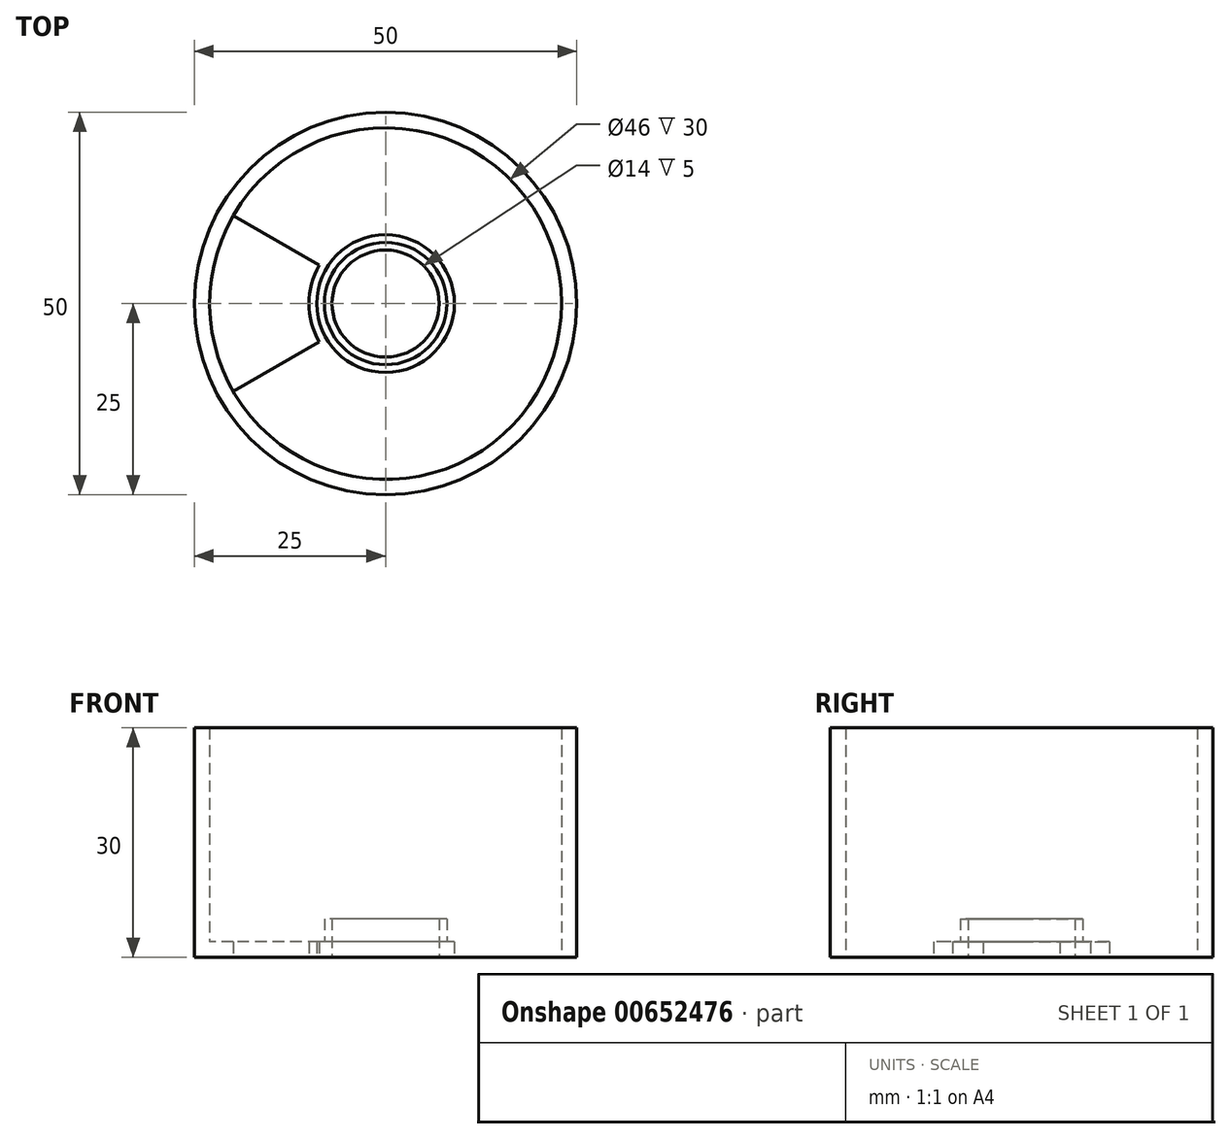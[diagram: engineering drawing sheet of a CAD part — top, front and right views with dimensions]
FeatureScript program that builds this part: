
annotation { "Feature Type Name" : "Feature", "Feature Type Description" : "" }
export const myFeature = defineFeature(function(context is Context, id is Id, definition is map)
    precondition{}
    {
        {
            var Q0;
            Q0=qCreatedBy(makeId("Top.planeOp"),FACE);
            var sketch = newSketch(context, id + "F0", { "sketchPlane" : qUnion([Q0])});
            skCircle(sketch, "E0", {"center": v(0, 0) * mm, "radius": 23 * mm});
            skCircle(sketch, "E1", {"center": v(0, 0) * mm, "radius": 25 * mm});
            skArc(sketch, "E2", {"start": v(-8.66, -5) * mm, "mid": v(-10, 0) * mm, "end": v(-8.66, 5) * mm});
            skLineSegment(sketch, "E3", {"start": v(-8.66, 5) * mm, "end": v(-19.92, 11.5) * mm});
            skLineSegment(sketch, "E4", {"start": v(-8.66, -5) * mm, "end": v(-19.92, -11.5) * mm});
            skCircle(sketch, "E5", {"center": v(0, 0) * mm, "radius": 7 * mm});
            skCircle(sketch, "E6", {"center": v(0, 0) * mm, "radius": 8 * mm});
            skCircle(sketch, "E7", {"center": v(0, 0) * mm, "radius": 9 * mm});
            skArc(sketch, "E8", {"start": v(-18.19, 10.5) * mm, "mid": v(-21, 0) * mm, "end": v(-18.19, -10.5) * mm});
            skSolve(sketch);
        }
        {
            var Q0;
            Q0=makeQuery(id+"F0.imprint","IMPRINT",FACE,{"disambiguationData":[TD([[makeQuery(id+"F0.imprint","IMPRINT",EDGE,{"derivedFrom":sQuery(id+"F0.wireOp",EDGE,"E2")}),-1.0]])]});
            var Q1;
            Q1=makeQuery(id+"F0.imprint","IMPRINT",FACE,{"disambiguationData":[TD([[makeQuery(id+"F0.imprint","IMPRINT",EDGE,{"derivedFrom":sQuery(id+"F0.wireOp",EDGE,"E6")}),-1.0]])]});
            var Q2;
            {var subQ5=sQuery(id+"F0.wireOp",EDGE,"E8");Q2=makeQuery(id+"F0.imprint","IMPRINT",FACE,{"disambiguationData":[TD([[makeQuery(id+"F0.imprint","IMPRINT",EDGE,{"derivedFrom":subQ5}),-1.0]])]});}
            extrude(context, id + "F1", {"entities" : qUnion([Q0, Q1, Q2]), "depth" : 2 * mm, "offsetDistance" : 25 * mm});
        }
        {
            var Q0;
            Q0=makeQuery(id+"F0.imprint","IMPRINT",FACE,{"disambiguationData":[TD([[makeQuery(id+"F0.imprint","IMPRINT",EDGE,{"derivedFrom":sQuery(id+"F0.wireOp",EDGE,"E5")}),-1.0]])]});
            extrude(context, id + "F2", {"entities" : qUnion([Q0]), "operationType" : NewBodyOperationType.ADD, "depth" : 5 * mm, "offsetDistance" : 25 * mm});
        }
        {
            var Q0;
            Q0=makeQuery(id+"F0.imprint","IMPRINT",FACE,{"disambiguationData":[TD([[makeQuery(id+"F0.imprint","IMPRINT",EDGE,{"derivedFrom":sQuery(id+"F0.wireOp",EDGE,"E1")}),1.0]])]});
            extrude(context, id + "F3", {"entities" : qUnion([Q0]), "operationType" : NewBodyOperationType.ADD, "depth" : 30 * mm, "offsetDistance" : 25 * mm});
        }
    });
